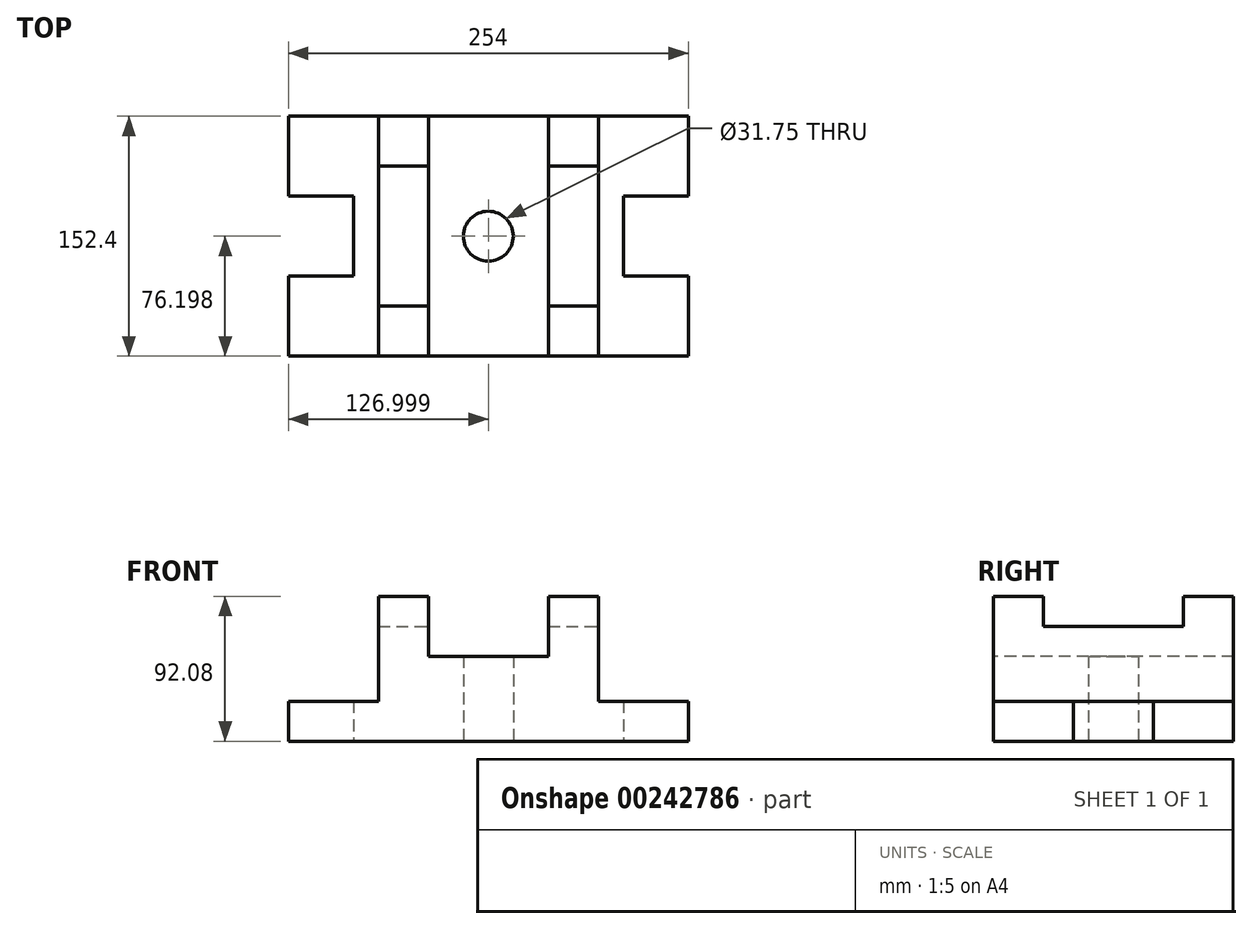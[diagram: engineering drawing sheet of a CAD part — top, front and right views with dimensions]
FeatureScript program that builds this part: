
annotation { "Feature Type Name" : "Feature", "Feature Type Description" : "" }
export const myFeature = defineFeature(function(context is Context, id is Id, definition is map)
    precondition{}
    {
        {
            var Q0;
            Q0=qCreatedBy(makeId("Top.planeOp"),FACE);
            var sketch = newSketch(context, id + "F0", { "sketchPlane" : qUnion([Q0])});
            skLineSegment(sketch, "E0.bottom", {"start": v(-132.73, 77.52) * mm, "end": v(121.27, 77.52) * mm});
            skLineSegment(sketch, "E0.top", {"start": v(-132.73, -74.88) * mm, "end": v(121.27, -74.88) * mm});
            skLineSegment(sketch, "E0.left", {"start": v(-132.73, 77.52) * mm, "end": v(-132.73, -74.88) * mm});
            skLineSegment(sketch, "E0.right", {"start": v(121.27, 77.52) * mm, "end": v(121.27, -74.88) * mm});
            skCircle(sketch, "E1", {"center": v(-5.73, 1.32) * mm, "radius": 15.88 * mm});
            skLineSegment(sketch, "E2", {"start": v(121.27, 26.72) * mm, "end": v(80, 26.72) * mm});
            skLineSegment(sketch, "E3", {"start": v(80, 26.72) * mm, "end": v(80, -24.08) * mm});
            skLineSegment(sketch, "E4", {"start": v(80, -24.08) * mm, "end": v(121.27, -24.08) * mm});
            skLineSegment(sketch, "E5", {"start": v(-132.73, 26.72) * mm, "end": v(-91.46, 26.72) * mm});
            skLineSegment(sketch, "E6", {"start": v(-91.46, 26.72) * mm, "end": v(-91.46, -24.08) * mm});
            skLineSegment(sketch, "E7", {"start": v(-91.46, -24.08) * mm, "end": v(-132.73, -24.08) * mm});
            skLineSegment(sketch, "E8", {"start": v(-43.83, 77.52) * mm, "end": v(-43.83, -74.88) * mm});
            skLineSegment(sketch, "E9", {"start": v(32.37, 77.52) * mm, "end": v(32.37, -74.88) * mm});
            skLineSegment(sketch, "E10", {"start": v(64.12, 77.52) * mm, "end": v(64.12, -74.88) * mm});
            skPoint(sketch, "E11.orphan", {"position": v(-5.73, 77.52) * mm});
            skPoint(sketch, "E12.end.orphan", {"position": v(-5.73, -74.88) * mm});
            skPoint(sketch, "E13.start.orphan", {"position": v(-132.73, 1.32) * mm});
            skPoint(sketch, "E14.orphan", {"position": v(121.27, 1.32) * mm});
            skLineSegment(sketch, "E15", {"start": v(-75.58, 77.52) * mm, "end": v(-75.58, 45.77) * mm});
            skLineSegment(sketch, "E16", {"start": v(-75.58, 45.77) * mm, "end": v(-43.83, 45.77) * mm});
            skLineSegment(sketch, "E17", {"start": v(-75.58, -74.88) * mm, "end": v(-75.58, -43.13) * mm});
            skLineSegment(sketch, "E18", {"start": v(-75.58, -43.13) * mm, "end": v(-43.83, -43.13) * mm});
            skLineSegment(sketch, "E19", {"start": v(32.37, 45.77) * mm, "end": v(64.12, 45.77) * mm});
            skLineSegment(sketch, "E20", {"start": v(32.37, -43.13) * mm, "end": v(64.12, -43.13) * mm});
            skLineSegment(sketch, "E21", {"start": v(-75.58, 45.77) * mm, "end": v(-75.58, -43.13) * mm});
            skSolve(sketch);
        }
        {
            var Q0;
            {var subQ6=sQuery(id+"F0.wireOp",EDGE,"E5");Q0=makeQuery(id+"F0.imprint","IMPRINT",FACE,{"disambiguationData":[TD([[makeQuery(id+"F0.imprint","IMPRINT",EDGE,{"derivedFrom":subQ6}),1.0]])]});}
            var Q1;
            {var subQ0=sQuery(id+"F0.wireOp",EDGE,"E2");Q1=makeQuery(id+"F0.imprint","IMPRINT",FACE,{"disambiguationData":[TD([[makeQuery(id+"F0.imprint","IMPRINT",EDGE,{"derivedFrom":subQ0}),-1.0]])]});}
            extrude(context, id + "F1", {"entities" : qUnion([Q0, Q1]), "depth" : 25.4 * mm});
        }
        {
            var Q0;
            Q0=makeQuery(id+"F0.imprint","IMPRINT",FACE,{"disambiguationData":[TD([[makeQuery(id+"F0.imprint","IMPRINT",EDGE,{"derivedFrom":sQuery(id+"F0.wireOp",EDGE,"E1")}),-1.0]])]});
            extrude(context, id + "F2", {"entities" : qUnion([Q0]), "operationType" : NewBodyOperationType.ADD, "depth" : 53.97 * mm});
        }
        {
            var Q0;
            {var subQ0=sQuery(id+"F0.wireOp",EDGE,"E16");Q0=makeQuery(id+"F0.imprint","IMPRINT",FACE,{"disambiguationData":[TD([[makeQuery(id+"F0.imprint","IMPRINT",EDGE,{"derivedFrom":subQ0}),-1.0]])]});}
            var Q1;
            {var subQ0=sQuery(id+"F0.wireOp",EDGE,"E19");Q1=makeQuery(id+"F0.imprint","IMPRINT",FACE,{"disambiguationData":[TD([[makeQuery(id+"F0.imprint","IMPRINT",EDGE,{"derivedFrom":subQ0}),-1.0]])]});}
            extrude(context, id + "F3", {"entities" : qUnion([Q0, Q1]), "operationType" : NewBodyOperationType.ADD, "depth" : 73.02 * mm});
        }
        {
            var Q0;
            {var subQ0=sQuery(id+"F0.wireOp",EDGE,"9GXIbx7K-8GZJ-heLD-PGIW-LZ1bsS0oICSi");Q0=makeQuery(id+"F0.imprint","IMPRINT",FACE,{"disambiguationData":[TD([[makeQuery(id+"F0.imprint","IMPRINT",EDGE,{"derivedFrom":subQ0}),-1.0]])]});}
            var Q1;
            {var subQ0=sQuery(id+"F0.wireOp",EDGE,"E0.bottom");Q1=makeQuery(id+"F0.imprint","IMPRINT",FACE,{"disambiguationData":[TD([[makeQuery(id+"F0.imprint","IMPRINT",EDGE,{"derivedFrom":subQ0}),-1.0]])]});}
            var Q2;
            {var subQ5=sQuery(id+"F0.wireOp",EDGE,"E20");Q2=makeQuery(id+"F0.imprint","IMPRINT",FACE,{"disambiguationData":[TD([[makeQuery(id+"F0.imprint","IMPRINT",EDGE,{"derivedFrom":subQ5}),-1.0]])]});}
            var Q3;
            {var subQ3=sQuery(id+"F0.wireOp",EDGE,"E17");Q3=makeQuery(id+"F0.imprint","IMPRINT",FACE,{"disambiguationData":[TD([[makeQuery(id+"F0.imprint","IMPRINT",EDGE,{"derivedFrom":subQ3}),-1.0]])]});}
            extrude(context, id + "F4", {"entities" : qUnion([Q0, Q1, Q2, Q3]), "operationType" : NewBodyOperationType.ADD, "depth" : 92.07 * mm});
        }
    });
